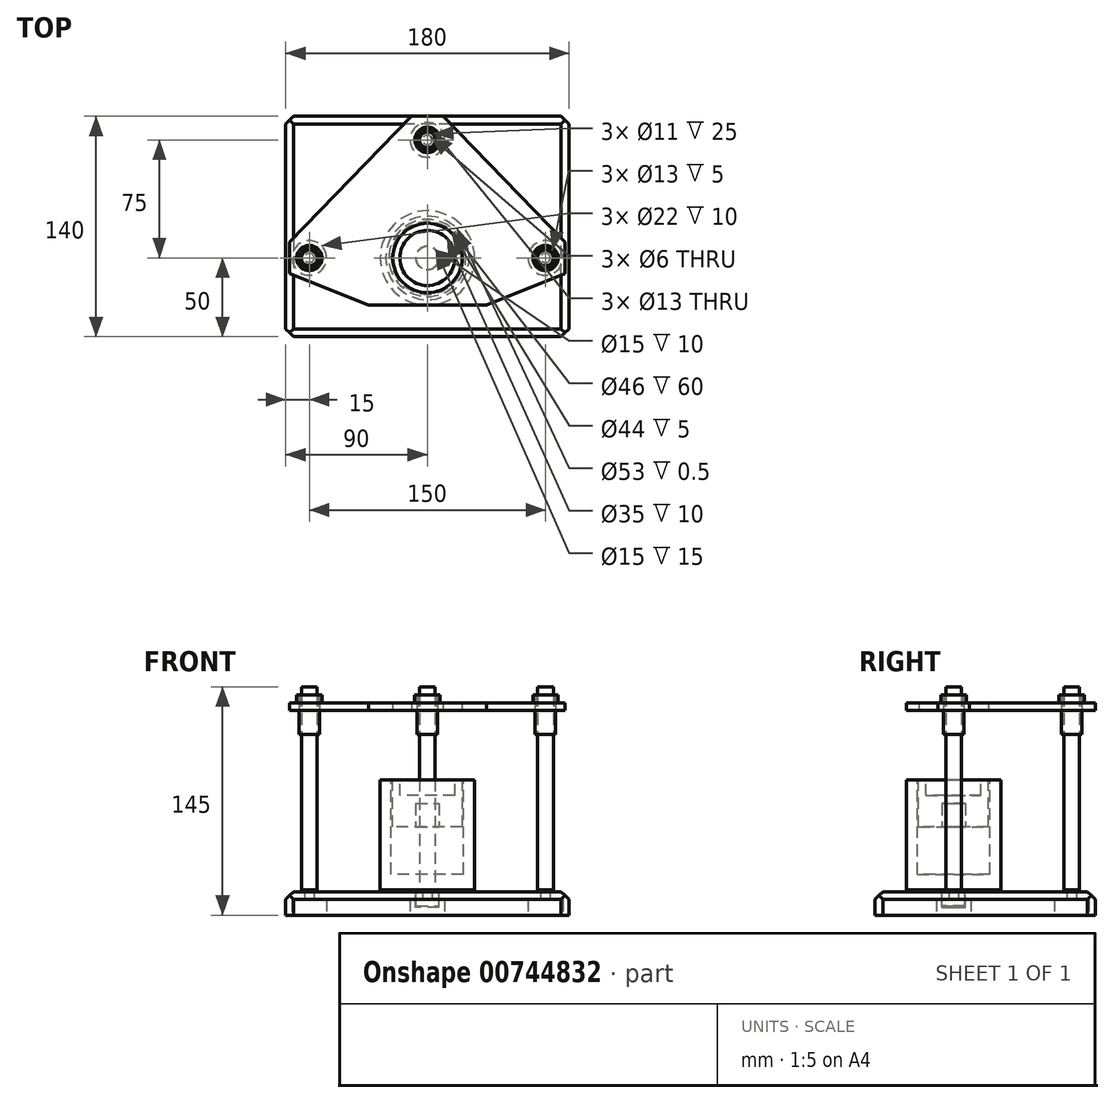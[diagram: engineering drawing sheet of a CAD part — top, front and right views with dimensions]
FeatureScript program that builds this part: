
annotation { "Feature Type Name" : "Feature", "Feature Type Description" : "" }
export const myFeature = defineFeature(function(context is Context, id is Id, definition is map)
    precondition{}
    {
        {
            var Q0;
            Q0=qCreatedBy(makeId("Top.planeOp"),FACE);
            var sketch = newSketch(context, id + "F0", { "sketchPlane" : qUnion([Q0])});
            skLineSegment(sketch, "E0.bottom", {"start": v(-90, 90) * mm, "end": v(90, 90) * mm});
            skLineSegment(sketch, "E0.top", {"start": v(-90, -50) * mm, "end": v(90, -50) * mm});
            skLineSegment(sketch, "E0.left", {"start": v(-90, 90) * mm, "end": v(-90, -50) * mm});
            skLineSegment(sketch, "E0.right", {"start": v(90, 90) * mm, "end": v(90, -50) * mm});
            skLineSegment(sketch, "E1", {"start": v(-116.55, 0) * mm, "end": v(184.4, 0) * mm, "construction": true});
            skLineSegment(sketch, "E2", {"start": v(0, -116.64) * mm, "end": v(0, 132.47) * mm, "construction": true});
            skCircle(sketch, "E3", {"center": v(0, 0) * mm, "radius": 25 * mm, "construction": true});
            skSolve(sketch);
        }
        {
            var Q0;
            Q0 = qSketchRegion(id + "F0", true);
            extrude(context, id + "F1", {"entities" : qUnion([Q0]), "depth" : 15 * mm, "offsetDistance" : 25 * mm});
        }
        {
            var Q0;
            Q0=makeQuery(id+"F0.imprint","IMPRINT",FACE,{"disambiguationData":[TD([[makeQuery(id+"F0.imprint","IMPRINT",EDGE,{"derivedFrom":sQuery(id+"F0.wireOp",EDGE,"E0.bottom")}),-1.0]])]});
            var sketch = newSketch(context, id + "F2", { "sketchPlane" : qUnion([Q0])});
            skCircle(sketch, "E4", {"center": v(-75, 0) * mm, "radius": 11 * mm});
            skCircle(sketch, "E5.1.0", {"center": v(0, 75) * mm, "radius": 11 * mm});
            skCircle(sketch, "E5.2.0", {"center": v(75, 0) * mm, "radius": 11 * mm});
            skPoint(sketch, "E5.center", {"position": v(0, 0) * mm});
            skLineSegment(sketch, "E5.anchor1", {"start": v(0, 0) * mm, "end": v(-75, 0) * mm, "construction": true});
            skLineSegment(sketch, "E5.anchor2", {"start": v(0, 0) * mm, "end": v(75, 0) * mm, "construction": true});
            skSolve(sketch);
        }
        {
            var Q0;
            Q0 = qSketchRegion(id + "F2", true);
            extrude(context, id + "F3", {"entities" : qUnion([Q0]), "operationType" : NewBodyOperationType.REMOVE, "depth" : 10 * mm, "offsetDistance" : 25 * mm});
        }
        {
            var Q0;
            Q0=makeQuery(id+"F0.imprint","IMPRINT",FACE,{"disambiguationData":[TD([[makeQuery(id+"F0.imprint","IMPRINT",EDGE,{"derivedFrom":sQuery(id+"F0.wireOp",EDGE,"E0.bottom")}),-1.0]])]});
            var sketch = newSketch(context, id + "F4", { "sketchPlane" : qUnion([Q0])});
            skCircle(sketch, "E6", {"center": v(-75, 0) * mm, "radius": 3 * mm});
            skCircle(sketch, "E7.1.0", {"center": v(0, 75) * mm, "radius": 3 * mm});
            skCircle(sketch, "E7.2.0", {"center": v(75, 0) * mm, "radius": 3 * mm});
            skPoint(sketch, "E7.center", {"position": v(0, 0) * mm});
            skLineSegment(sketch, "E7.anchor1", {"start": v(0, 0) * mm, "end": v(-75, 0) * mm, "construction": true});
            skLineSegment(sketch, "E7.anchor2", {"start": v(0, 0) * mm, "end": v(75, 0) * mm, "construction": true});
            skSolve(sketch);
        }
        {
            var Q0;
            Q0 = qSketchRegion(id + "F4", true);
            var Q1;
            Q1=makeQuery(id+"F1.opExtrude","CAP_FACE",FACE,{"disambiguationData":[OSD([sQuery(id+"F0.wireOp",EDGE,"E0.bottom"),sQuery(id+"F0.wireOp",EDGE,"E0.top"),sQuery(id+"F0.wireOp",EDGE,"E0.left"),sQuery(id+"F0.wireOp",EDGE,"E0.right")])],"isStart":false});
            extrude(context, id + "F5", {"entities" : qUnion([Q0]), "operationType" : NewBodyOperationType.REMOVE, "endBound" : BoundingType.UP_TO_SURFACE, "depth" : 25 * mm, "endBoundEntityFace" : qUnion([Q1]), "offsetDistance" : 25 * mm});
        }
        {
            var Q0;
            Q0=makeQuery(id+"F1.opExtrude","CAP_FACE",FACE,{"disambiguationData":[OSD([sQuery(id+"F0.wireOp",EDGE,"E0.bottom"),sQuery(id+"F0.wireOp",EDGE,"E0.top"),sQuery(id+"F0.wireOp",EDGE,"E0.left"),sQuery(id+"F0.wireOp",EDGE,"E0.right")])],"isStart":false});
            var sketch = newSketch(context, id + "F6", { "sketchPlane" : qUnion([Q0])});
            skCircle(sketch, "E8", {"center": v(0, 0) * mm, "radius": 7.5 * mm});
            skSolve(sketch);
        }
        {
            var Q0;
            Q0 = qSketchRegion(id + "F6", true);
            extrude(context, id + "F7", {"entities" : qUnion([Q0]), "operationType" : NewBodyOperationType.REMOVE, "oppositeDirection" : true, "depth" : 10 * mm, "offsetDistance" : 25 * mm});
        }
        {
            var Q0;
            Q0=qCreatedBy(makeId("Top.planeOp"),FACE);
            var sketch = newSketch(context, id + "F8", { "sketchPlane" : qUnion([Q0])});
            skLineSegment(sketch, "E9.bottom", {"start": v(37.5, -30) * mm, "end": v(-37.5, -30) * mm});
            skLineSegment(sketch, "E9.top", {"start": v(10, 90) * mm, "end": v(-10, 90) * mm});
            skLineSegment(sketch, "E9.left", {"start": v(87.5, -10) * mm, "end": v(87.5, 10) * mm});
            skLineSegment(sketch, "E9.right", {"start": v(-87.5, -10) * mm, "end": v(-87.5, 10) * mm});
            skLineSegment(sketch, "E10", {"start": v(0, 100.44) * mm, "end": v(0, -100.88) * mm, "construction": true});
            skLineSegment(sketch, "E11", {"start": v(-110.9, 0) * mm, "end": v(146.21, 0) * mm, "construction": true});
            skCircle(sketch, "E12", {"center": v(0, 0) * mm, "radius": 22 * mm});
            skLineSegment(sketch, "E13", {"start": v(-10, 90) * mm, "end": v(-87.5, 10) * mm});
            skLineSegment(sketch, "E14.MirrorCS", {"start": v(10, 90) * mm, "end": v(87.5, 10) * mm});
            skLineSegment(sketch, "E15", {"start": v(-87.5, -10) * mm, "end": v(-37.5, -30) * mm});
            skLineSegment(sketch, "E16.MirrorCS", {"start": v(87.5, -10) * mm, "end": v(37.5, -30) * mm});
            skPoint(sketch, "E17.orphan", {"position": v(-87.5, -30) * mm});
            skCircle(sketch, "E18", {"center": v(-75, 0) * mm, "radius": 6.5 * mm});
            skCircle(sketch, "E19.1.0", {"center": v(0, 75) * mm, "radius": 6.5 * mm});
            skCircle(sketch, "E19.2.0", {"center": v(75, 0) * mm, "radius": 6.5 * mm});
            skLineSegment(sketch, "E19.anchor1", {"start": v(0, 0) * mm, "end": v(-75, 0) * mm, "construction": true});
            skLineSegment(sketch, "E19.anchor2", {"start": v(0, 0) * mm, "end": v(75, 0) * mm, "construction": true});
            skSolve(sketch);
        }
        {
            var Q0;
            Q0 = qSketchRegion(id + "F8", true);
            extrude(context, id + "F9", {"entities" : qUnion([Q0]), "depth" : 135 * mm, "offsetDistance" : 25 * mm, "hasSecondDirection" : true, "secondDirectionOppositeDirection" : false, "secondDirectionDepth" : 130 * mm});
        }
        {
            var Q0;
            Q0=qCreatedBy(makeId("Front.planeOp"),FACE);
            var sketch = newSketch(context, id + "F10", { "sketchPlane" : qUnion([Q0])});
            skLineSegment(sketch, "E20", {"start": v(0, 130) * mm, "end": v(-26.5, 130) * mm, "construction": true});
            skLineSegment(sketch, "E21", {"start": v(0, 83.98) * mm, "end": v(0, 110.3) * mm, "construction": true});
            skPoint(sketch, "E21.endSnap0", {"position": v(0, 135) * mm});
            skLineSegment(sketch, "E22", {"start": v(-26.5, 130) * mm, "end": v(-24.5, 130) * mm});
            skPoint(sketch, "E23.center.orphan", {"position": v(-25.5, 130) * mm});
            skLineSegment(sketch, "E24", {"start": v(-27.5, 130) * mm, "end": v(-24.5, 130) * mm});
            skLineSegment(sketch, "E25", {"start": v(-23.5, 101.47) * mm, "end": v(-23.5, 130) * mm, "construction": true});
            skLineSegment(sketch, "E26", {"start": v(-26.5, 130) * mm, "end": v(-26.5, 130.5) * mm});
            skLineSegment(sketch, "E27", {"start": v(-26.5, 130.5) * mm, "end": v(-24.5, 130.5) * mm});
            skLineSegment(sketch, "E28", {"start": v(-24.5, 130.5) * mm, "end": v(-24.5, 130) * mm});
            skPoint(sketch, "E29.start.orphan", {"position": v(-26.5, 101) * mm});
            skLineSegment(sketch, "E30.trimOffspring", {"start": v(-27.5, 130) * mm, "end": v(-40.27, 130) * mm, "construction": true});
            skSolve(sketch);
        }
        {
            var Q0;
            Q0 = qSketchRegion(id + "F10", true);
            var Q1;
            Q1=sQuery(id+"F10.wireOp",EDGE,"E21");
            revolve(context, id + "F11", {"operationType" : NewBodyOperationType.REMOVE, "surfaceOperationType" : NewSurfaceOperationType.NEW, "entities" : qUnion([Q0]), "axis" : qUnion([Q1]), "revolveType" : RevolveType.FULL, "oppositeDirection" : true});
        }
        {
            var Q0;
            Q0=makeQuery(id+"F6.imprint","IMPRINT",FACE,{"disambiguationData":[TD([[makeQuery(id+"F6.imprint","IMPRINT",EDGE,{"derivedFrom":sQuery(id+"F6.wireOp",EDGE,"E8")}),-1.0]])]});
            var sketch = newSketch(context, id + "F12", { "sketchPlane" : qUnion([Q0])});
            skCircle(sketch, "E31", {"center": v(0, 0) * mm, "radius": 30 * mm});
            skSolve(sketch);
        }
        {
            var Q0;
            Q0 = qSketchRegion(id + "F12", true);
            extrude(context, id + "F13", {"entities" : qUnion([Q0]), "depth" : 71 * mm, "offsetDistance" : 25 * mm, "hasSecondDirection" : true, "secondDirectionOppositeDirection" : false, "secondDirectionDepth" : 1 * mm});
        }
        {
            var Q0;
            Q0=makeQuery(id+"F13.opExtrude","CAP_FACE",FACE,{"disambiguationData":[OSD([sQuery(id+"F12.wireOp",EDGE,"E31")])],"isStart":true});
            var sketch = newSketch(context, id + "F14", { "sketchPlane" : qUnion([Q0])});
            skCircle(sketch, "E32", {"center": v(0, 0) * mm, "radius": 7.25 * mm});
            skSolve(sketch);
        }
        {
            var Q0;
            Q0 = qSketchRegion(id + "F14", true);
            extrude(context, id + "F15", {"entities" : qUnion([Q0]), "operationType" : NewBodyOperationType.ADD, "depth" : 10 * mm, "offsetDistance" : 25 * mm});
        }
        {
            var Q0;
            Q0=makeQuery(id+"F13.opExtrude","CAP_FACE",FACE,{"disambiguationData":[OSD([sQuery(id+"F12.wireOp",EDGE,"E31")])],"isStart":false});
            var sketch = newSketch(context, id + "F16", { "sketchPlane" : qUnion([Q0])});
            skCircle(sketch, "E33", {"center": v(0, 0) * mm, "radius": 23 * mm});
            skSolve(sketch);
        }
        {
            var Q0;
            Q0 = qSketchRegion(id + "F16", true);
            extrude(context, id + "F17", {"entities" : qUnion([Q0]), "operationType" : NewBodyOperationType.REMOVE, "oppositeDirection" : true, "depth" : 60 * mm, "offsetDistance" : 25 * mm});
        }
        {
            var Q0;
            Q0=makeQuery(id+"F9.opExtrude","CAP_FACE",FACE,{"disambiguationData":[OSD([sQuery(id+"F8.wireOp",EDGE,"E9.bottom"),sQuery(id+"F8.wireOp",EDGE,"E9.top"),sQuery(id+"F8.wireOp",EDGE,"E9.left"),sQuery(id+"F8.wireOp",EDGE,"E9.right"),sQuery(id+"F8.wireOp",EDGE,"E12"),sQuery(id+"F8.wireOp",EDGE,"E13"),sQuery(id+"F8.wireOp",EDGE,"E14.MirrorCS"),sQuery(id+"F8.wireOp",EDGE,"E15"),sQuery(id+"F8.wireOp",EDGE,"E16.MirrorCS"),sQuery(id+"F8.wireOp",EDGE,"E18"),sQuery(id+"F8.wireOp",EDGE,"E19.1.0"),sQuery(id+"F8.wireOp",EDGE,"E19.2.0")])],"isStart":false});
            var sketch = newSketch(context, id + "F18", { "sketchPlane" : qUnion([Q0])});
            skCircle(sketch, "E34", {"center": v(-75, 0) * mm, "radius": 6.5 * mm});
            skCircle(sketch, "E35.1.0", {"center": v(0, 75) * mm, "radius": 6.5 * mm});
            skCircle(sketch, "E35.2.0", {"center": v(75, 0) * mm, "radius": 6.5 * mm});
            skPoint(sketch, "E35.center", {"position": v(0, 0) * mm});
            skLineSegment(sketch, "E35.anchor1", {"start": v(0, 0) * mm, "end": v(-75, 0) * mm, "construction": true});
            skLineSegment(sketch, "E35.anchor2", {"start": v(0, 0) * mm, "end": v(75, 0) * mm, "construction": true});
            skCircle(sketch, "E36", {"center": v(-75, 0) * mm, "radius": 5.5 * mm});
            skCircle(sketch, "E37.1.0", {"center": v(0, 75) * mm, "radius": 5.5 * mm});
            skCircle(sketch, "E37.2.0", {"center": v(75, 0) * mm, "radius": 5.5 * mm});
            skSolve(sketch);
        }
        {
            var Q0;
            Q0 = qSketchRegion(id + "F18", true);
            extrude(context, id + "F19", {"entities" : qUnion([Q0]), "depth" : 5 * mm, "offsetDistance" : 25 * mm, "hasSecondDirection" : true, "secondDirectionOppositeDirection" : true, "secondDirectionDepth" : 20 * mm});
        }
        {
            var Q0;
            Q0=makeQuery(id+"F1.opExtrude","CAP_EDGE",EDGE,{"disambiguationData":[OSD([sQuery(id+"F0.wireOp",EDGE,"E0.top")])],"isStart":false});
            var Q1;
            Q1=makeQuery(id+"F1.opExtrude","CAP_EDGE",EDGE,{"disambiguationData":[OSD([sQuery(id+"F0.wireOp",EDGE,"E0.right")])],"isStart":false});
            var Q2;
            Q2=makeQuery(id+"F1.opExtrude","CAP_EDGE",EDGE,{"disambiguationData":[OSD([sQuery(id+"F0.wireOp",EDGE,"E0.bottom")])],"isStart":false});
            var Q3;
            Q3=makeQuery(id+"F1.opExtrude","CAP_EDGE",EDGE,{"disambiguationData":[OSD([sQuery(id+"F0.wireOp",EDGE,"E0.left")])],"isStart":false});
            chamfer(context, id + "F20", {"entities" : qUnion([Q0, Q1, Q2, Q3]), "width" : 5 * mm, "tangentPropagation" : true});
        }
        {
            var Q0;
            Q0=makeQuery(id+"F1.opExtrude","SWEPT_EDGE",EDGE,{"disambiguationData":[OSD([sQuery(id+"F0.wireOp",EDGE,"E0.top"),sQuery(id+"F0.wireOp",EDGE,"E0.right")])]});
            var Q1;
            Q1=makeQuery(id+"F1.opExtrude","SWEPT_EDGE",EDGE,{"disambiguationData":[OSD([sQuery(id+"F0.wireOp",EDGE,"E0.bottom"),sQuery(id+"F0.wireOp",EDGE,"E0.right")])]});
            var Q2;
            Q2=makeQuery(id+"F1.opExtrude","SWEPT_EDGE",EDGE,{"disambiguationData":[OSD([sQuery(id+"F0.wireOp",EDGE,"E0.top"),sQuery(id+"F0.wireOp",EDGE,"E0.left")])]});
            var Q3;
            Q3=makeQuery(id+"F1.opExtrude","SWEPT_EDGE",EDGE,{"disambiguationData":[OSD([sQuery(id+"F0.wireOp",EDGE,"E0.bottom"),sQuery(id+"F0.wireOp",EDGE,"E0.left")])]});
            chamfer(context, id + "F21", {"entities" : qUnion([Q0, Q1, Q2, Q3]), "width" : 5 * mm, "tangentPropagation" : true});
        }
        {
            var Q0;
            Q0=makeQuery(id+"F9.opExtrude","CAP_FACE",FACE,{"disambiguationData":[OSD([sQuery(id+"F8.wireOp",EDGE,"E9.bottom"),sQuery(id+"F8.wireOp",EDGE,"E9.top"),sQuery(id+"F8.wireOp",EDGE,"E9.left"),sQuery(id+"F8.wireOp",EDGE,"E9.right"),sQuery(id+"F8.wireOp",EDGE,"E12"),sQuery(id+"F8.wireOp",EDGE,"E13"),sQuery(id+"F8.wireOp",EDGE,"E14.MirrorCS"),sQuery(id+"F8.wireOp",EDGE,"E15"),sQuery(id+"F8.wireOp",EDGE,"E16.MirrorCS"),sQuery(id+"F8.wireOp",EDGE,"E18"),sQuery(id+"F8.wireOp",EDGE,"E19.1.0"),sQuery(id+"F8.wireOp",EDGE,"E19.2.0")])],"isStart":false});
            var sketch = newSketch(context, id + "F22", { "sketchPlane" : qUnion([Q0])});
            skCircle(sketch, "E38", {"center": v(-75, 0) * mm, "radius": 8 * mm});
            skCircle(sketch, "E39", {"center": v(-75, 0) * mm, "radius": 6.5 * mm});
            skCircle(sketch, "E40.1.0", {"center": v(0, 75) * mm, "radius": 8 * mm});
            skCircle(sketch, "E40.1.1", {"center": v(0, 75) * mm, "radius": 6.5 * mm});
            skCircle(sketch, "E40.2.0", {"center": v(75, 0) * mm, "radius": 8 * mm});
            skCircle(sketch, "E40.2.1", {"center": v(75, 0) * mm, "radius": 6.5 * mm});
            skPoint(sketch, "E40.center", {"position": v(0, 0) * mm});
            skLineSegment(sketch, "E40.anchor1", {"start": v(0, 0) * mm, "end": v(-75, 0) * mm, "construction": true});
            skLineSegment(sketch, "E40.anchor2", {"start": v(0, 0) * mm, "end": v(75, 0) * mm, "construction": true});
            skSolve(sketch);
        }
        {
            var Q0;
            Q0 = qSketchRegion(id + "F22", true);
            extrude(context, id + "F23", {"entities" : qUnion([Q0]), "depth" : 5 * mm, "offsetDistance" : 25 * mm});
        }
        {
            var Q0;
            Q0=makeQuery(id+"F13.opExtrude","CAP_FACE",FACE,{"disambiguationData":[OSD([sQuery(id+"F12.wireOp",EDGE,"E31")])],"isStart":false});
            var sketch = newSketch(context, id + "F24", { "sketchPlane" : qUnion([Q0])});
            skCircle(sketch, "E41", {"center": v(0, 0) * mm, "radius": 22.25 * mm});
            skSolve(sketch);
        }
        {
            var Q0;
            Q0 = qSketchRegion(id + "F24", true);
            extrude(context, id + "F25", {"entities" : qUnion([Q0]), "oppositeDirection" : true, "depth" : 30 * mm, "offsetDistance" : 25 * mm});
        }
        {
            var Q0;
            Q0=makeQuery(id+"F25.opExtrude","CAP_FACE",FACE,{"disambiguationData":[OSD([sQuery(id+"F24.wireOp",EDGE,"E41")])],"isStart":true});
            var sketch = newSketch(context, id + "F26", { "sketchPlane" : qUnion([Q0])});
            skCircle(sketch, "E42", {"center": v(0, 0) * mm, "radius": 17.5 * mm});
            skSolve(sketch);
        }
        {
            var Q0;
            Q0 = qSketchRegion(id + "F26", true);
            extrude(context, id + "F27", {"entities" : qUnion([Q0]), "operationType" : NewBodyOperationType.REMOVE, "oppositeDirection" : true, "depth" : 10 * mm, "offsetDistance" : 25 * mm});
        }
        {
            var Q0;
            Q0=makeQuery(id+"F25.opExtrude","CAP_FACE",FACE,{"disambiguationData":[OSD([sQuery(id+"F24.wireOp",EDGE,"E41")])],"isStart":false});
            var sketch = newSketch(context, id + "F28", { "sketchPlane" : qUnion([Q0])});
            skCircle(sketch, "E43", {"center": v(0, 0) * mm, "radius": 7.5 * mm});
            skSolve(sketch);
        }
        {
            var Q0;
            Q0 = qSketchRegion(id + "F28", true);
            extrude(context, id + "F29", {"entities" : qUnion([Q0]), "operationType" : NewBodyOperationType.REMOVE, "oppositeDirection" : true, "depth" : 15 * mm, "offsetDistance" : 25 * mm});
        }
        {
            var Q0;
            Q0=makeQuery(id+"F1.opExtrude","CAP_FACE",FACE,{"disambiguationData":[OSD([sQuery(id+"F0.wireOp",EDGE,"E0.bottom"),sQuery(id+"F0.wireOp",EDGE,"E0.top"),sQuery(id+"F0.wireOp",EDGE,"E0.left"),sQuery(id+"F0.wireOp",EDGE,"E0.right")])],"isStart":false});
            var sketch = newSketch(context, id + "F30", { "sketchPlane" : qUnion([Q0])});
            skCircle(sketch, "E44", {"center": v(-75, 0) * mm, "radius": 5 * mm});
            skCircle(sketch, "E45.1.0", {"center": v(0, 75) * mm, "radius": 5 * mm});
            skCircle(sketch, "E45.2.0", {"center": v(75, 0) * mm, "radius": 5 * mm});
            skPoint(sketch, "E45.center", {"position": v(0, 0) * mm});
            skLineSegment(sketch, "E45.anchor1", {"start": v(0, 0) * mm, "end": v(-75, 0) * mm, "construction": true});
            skLineSegment(sketch, "E45.anchor2", {"start": v(0, 0) * mm, "end": v(75, 0) * mm, "construction": true});
            skSolve(sketch);
        }
        {
            var Q0;
            Q0 = qSketchRegion(id + "F30", true);
            extrude(context, id + "F31", {"entities" : qUnion([Q0]), "depth" : 130 * mm, "offsetDistance" : 25 * mm, "hasSecondDirection" : true, "secondDirectionOppositeDirection" : false, "secondDirectionDepth" : 1 * mm});
        }
    });
